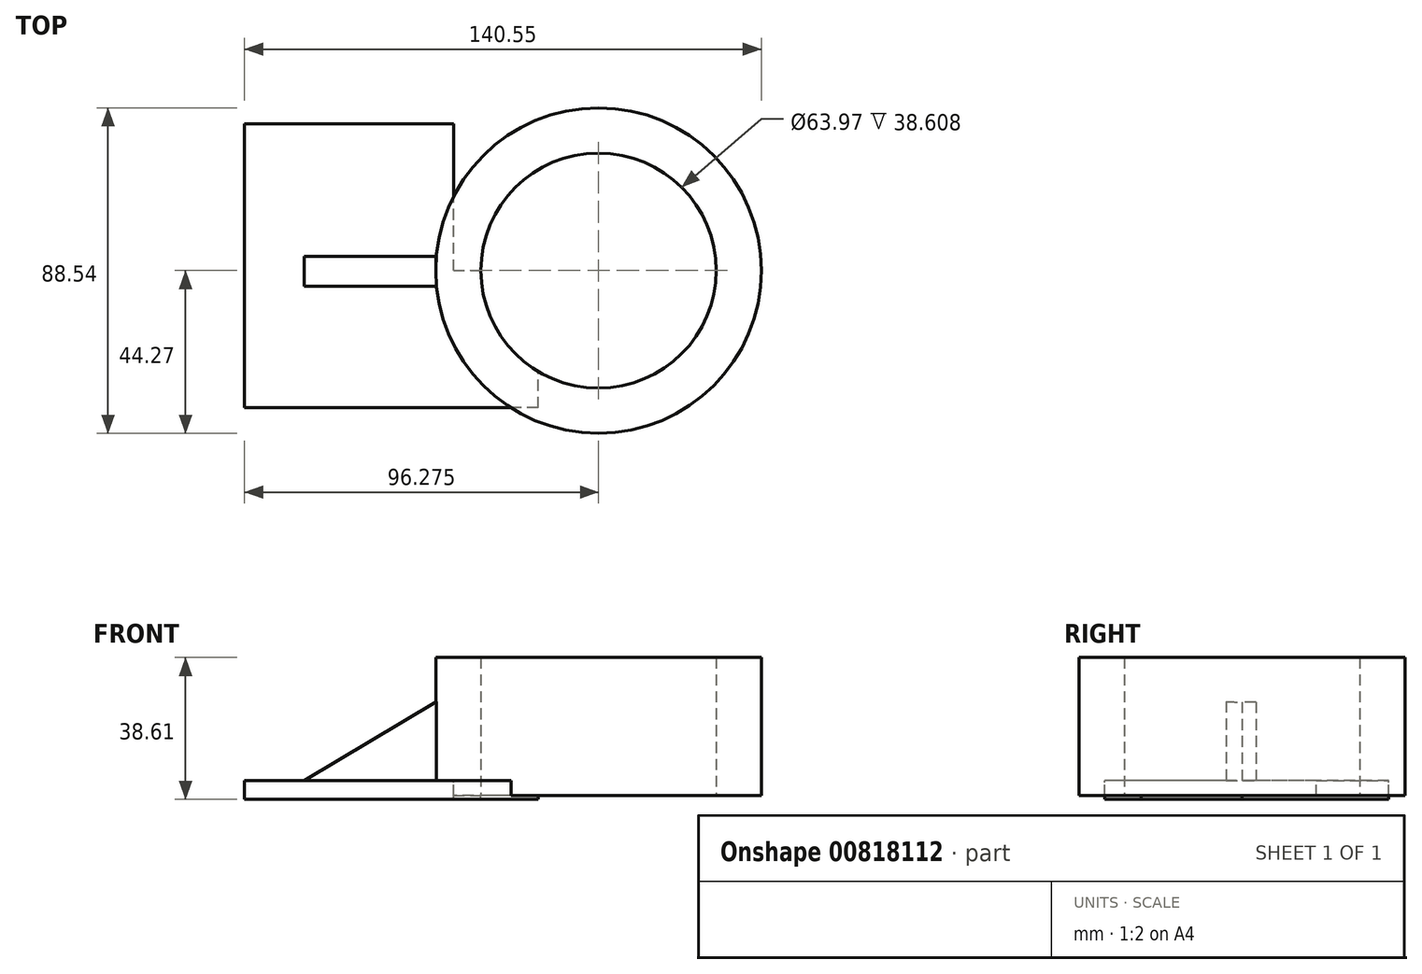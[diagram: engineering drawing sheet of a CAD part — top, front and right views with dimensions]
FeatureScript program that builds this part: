
annotation { "Feature Type Name" : "Feature", "Feature Type Description" : "" }
export const myFeature = defineFeature(function(context is Context, id is Id, definition is map)
    precondition{}
    {
        {
            var Q0;
            Q0=qCreatedBy(makeId("Top.planeOp"),FACE);
            var sketch = newSketch(context, id + "F0", { "sketchPlane" : qUnion([Q0])});
            skLineSegment(sketch, "E0.bottom", {"start": v(0, 0) * mm, "end": v(-56.86, 0) * mm});
            skLineSegment(sketch, "E0.top", {"start": v(0, 39.93) * mm, "end": v(-56.86, 39.93) * mm});
            skLineSegment(sketch, "E0.left", {"start": v(0, 0) * mm, "end": v(0, 39.93) * mm});
            skLineSegment(sketch, "E0.right", {"start": v(-56.86, 0) * mm, "end": v(-56.86, 39.93) * mm});
            skLineSegment(sketch, "E1.top", {"start": v(0, -37.33) * mm, "end": v(-56.86, -37.33) * mm});
            skLineSegment(sketch, "E1.left", {"start": v(0, 0) * mm, "end": v(0, -37.33) * mm});
            skLineSegment(sketch, "E1.right", {"start": v(-56.86, 0) * mm, "end": v(-56.86, -37.33) * mm});
            skLineSegment(sketch, "E2.bottom", {"start": v(0, -37.33) * mm, "end": v(23, -37.33) * mm});
            skLineSegment(sketch, "E2.top", {"start": v(0, 0) * mm, "end": v(23, 0) * mm});
            skLineSegment(sketch, "E2.left", {"start": v(0, -37.33) * mm, "end": v(0, 0) * mm});
            skLineSegment(sketch, "E2.right", {"start": v(23, -37.33) * mm, "end": v(23, 0) * mm});
            skLineSegment(sketch, "E3.bottom", {"start": v(23, 0) * mm, "end": v(0, 0) * mm});
            skLineSegment(sketch, "E3.top", {"start": v(23, 39.93) * mm, "end": v(0, 39.93) * mm});
            skLineSegment(sketch, "E3.left", {"start": v(23, 0) * mm, "end": v(23, 39.93) * mm});
            skSolve(sketch);
        }
        {
            var Q0;
            Q0=makeQuery(id+"F0.imprint","IMPRINT",FACE,{"disambiguationData":[TD([[makeQuery(id+"F0.imprint","IMPRINT",EDGE,{"derivedFrom":sQuery(id+"F0.wireOp",EDGE,"E0.bottom")}),1.0]])]});
            var Q1;
            Q1=makeQuery(id+"F0.imprint","IMPRINT",FACE,{"disambiguationData":[TD([[makeQuery(id+"F0.imprint","IMPRINT",EDGE,{"derivedFrom":sQuery(id+"F0.wireOp",EDGE,"E0.top")}),1.0]])]});
            var Q2;
            Q2=makeQuery(id+"F0.imprint","IMPRINT",FACE,{"disambiguationData":[TD([[makeQuery(id+"F0.imprint","IMPRINT",EDGE,{"derivedFrom":sQuery(id+"F0.wireOp",EDGE,"E3.bottom")}),-1.0]])]});
            var Q3;
            Q3=makeQuery(id+"F0.imprint","IMPRINT",FACE,{"disambiguationData":[TD([[makeQuery(id+"F0.imprint","IMPRINT",EDGE,{"derivedFrom":sQuery(id+"F0.wireOp",EDGE,"E2.bottom")}),1.0]])]});
            extrude(context, id + "F1", {"entities" : qUnion([Q0, Q1, Q2, Q3]), "oppositeDirection" : true, "depth" : 5.08 * mm, "offsetDistance" : 25.4 * mm});
        }
        {
            var Q0;
            Q0=makeQuery(id+"F1.opExtrude","CAP_FACE",FACE,{"disambiguationData":[OSD([sQuery(id+"F0.wireOp",EDGE,"E0.top"),sQuery(id+"F0.wireOp",EDGE,"E0.right"),sQuery(id+"F0.wireOp",EDGE,"E1.top"),sQuery(id+"F0.wireOp",EDGE,"E1.right"),sQuery(id+"F0.wireOp",EDGE,"E2.bottom"),sQuery(id+"F0.wireOp",EDGE,"E2.right"),sQuery(id+"F0.wireOp",EDGE,"E3.top"),sQuery(id+"F0.wireOp",EDGE,"E3.left")])],"isStart":true});
            var sketch = newSketch(context, id + "F2", { "sketchPlane" : qUnion([Q0])});
            skLineSegment(sketch, "E4", {"start": v(0, 0) * mm, "end": v(39.42, 0) * mm});
            skCircle(sketch, "E5", {"center": v(39.42, 0) * mm, "radius": 44.27 * mm});
            skCircle(sketch, "E6", {"center": v(39.42, 0) * mm, "radius": 31.98 * mm});
            skSolve(sketch);
        }
        {
            var Q0;
            Q0=qSketchRegion(id+"F2",true);
            var Q1;
            {var subQ0=sQuery(id+"F2.wireOp",EDGE,"E6");var subQ1=makeQuery(id+"F2.imprint","INTERSECT",VERTEX,{"derivedFrom":[sQuery(id+"F2.wireOp",EDGE,"E4"),subQ0]});Q1=makeQuery(id+"F2.imprint","IMPRINT",FACE,{"disambiguationData":[TD([[makeQuery(id+"F2.imprint","IMPRINT",EDGE,{"disambiguationData":[TD([[subQ1,1.0]])],"derivedFrom":subQ0}),-1.0]])]});}
            extrude(context, id + "F3", {"entities" : qUnion([Q0, Q1]), "operationType" : NewBodyOperationType.ADD, "depth" : 33.53 * mm, "offsetDistance" : 25.4 * mm});
        }
        {
            var Q0;
            Q0=makeQuery(id+"F3.opExtrude","CAP_FACE",FACE,{"disambiguationData":[OSD([sQuery(id+"F2.wireOp",EDGE,"E5"),sQuery(id+"F2.wireOp",EDGE,"E6")])],"isStart":true});
            extrude(context, id + "F4", {"entities" : qUnion([Q0]), "operationType" : NewBodyOperationType.ADD, "depth" : 4.06 * mm, "offsetDistance" : 25.4 * mm});
        }
        {
            var Q0;
            {var subQ0=sQuery(id+"F0.wireOp",EDGE,"E3.left");var subQ1=sQuery(id+"F0.wireOp",EDGE,"E2.right");var subQ2=sQuery(id+"F2.wireOp",EDGE,"E6");Q0=makeQuery(id+"F3.boolean.opBoolean","SPLIT",FACE,{"disambiguationData":[TD([makeQuery(id+"F3.opExtrude","SWEPT_FACE",FACE,{"disambiguationData":[OSD([subQ2])]})])],"derivedFrom":makeQuery(id+"F1.opExtrude","CAP_FACE",FACE,{"disambiguationData":[OSD([sQuery(id+"F0.wireOp",EDGE,"E0.top"),sQuery(id+"F0.wireOp",EDGE,"E0.right"),sQuery(id+"F0.wireOp",EDGE,"E1.top"),sQuery(id+"F0.wireOp",EDGE,"E1.right"),sQuery(id+"F0.wireOp",EDGE,"E2.bottom"),subQ1,sQuery(id+"F0.wireOp",EDGE,"E3.top"),subQ0])],"isStart":true})});}
            extrude(context, id + "F5", {"entities" : qUnion([Q0]), "operationType" : NewBodyOperationType.REMOVE, "oppositeDirection" : true, "depth" : 123.7 * mm, "offsetDistance" : 25.4 * mm});
        }
        {
            var Q0;
            Q0=qCreatedBy(makeId("Front.planeOp"),FACE);
            var sketch = newSketch(context, id + "F6", { "sketchPlane" : qUnion([Q0])});
            skLineSegment(sketch, "E7", {"start": v(0, 0) * mm, "end": v(0, 24.3) * mm});
            skLineSegment(sketch, "E8", {"start": v(0, 24.3) * mm, "end": v(-40.67, 0) * mm});
            skLineSegment(sketch, "E9", {"start": v(-40.67, 0) * mm, "end": v(0, 0) * mm});
            skSolve(sketch);
        }
        {
            var Q0;
            Q0=makeQuery(id+"F6.imprint","IMPRINT",FACE,{"disambiguationData":[TD([[makeQuery(id+"F6.imprint","IMPRINT",EDGE,{"derivedFrom":sQuery(id+"F6.wireOp",EDGE,"E7")}),1.0]])]});
            extrude(context, id + "F7", {"entities" : qUnion([Q0]), "operationType" : NewBodyOperationType.ADD, "depth" : 4.32 * mm, "offsetDistance" : 25.4 * mm});
        }
        {
            var Q0;
            Q0=makeQuery(id+"F7.opExtrude","CAP_FACE",FACE,{"disambiguationData":[OSD([sQuery(id+"F6.wireOp",EDGE,"E7"),sQuery(id+"F6.wireOp",EDGE,"E8"),sQuery(id+"F6.wireOp",EDGE,"E9")])],"isStart":true});
            extrude(context, id + "F8", {"entities" : qUnion([Q0]), "operationType" : NewBodyOperationType.ADD, "depth" : 3.8 * mm, "offsetDistance" : 25.4 * mm});
        }
    });
